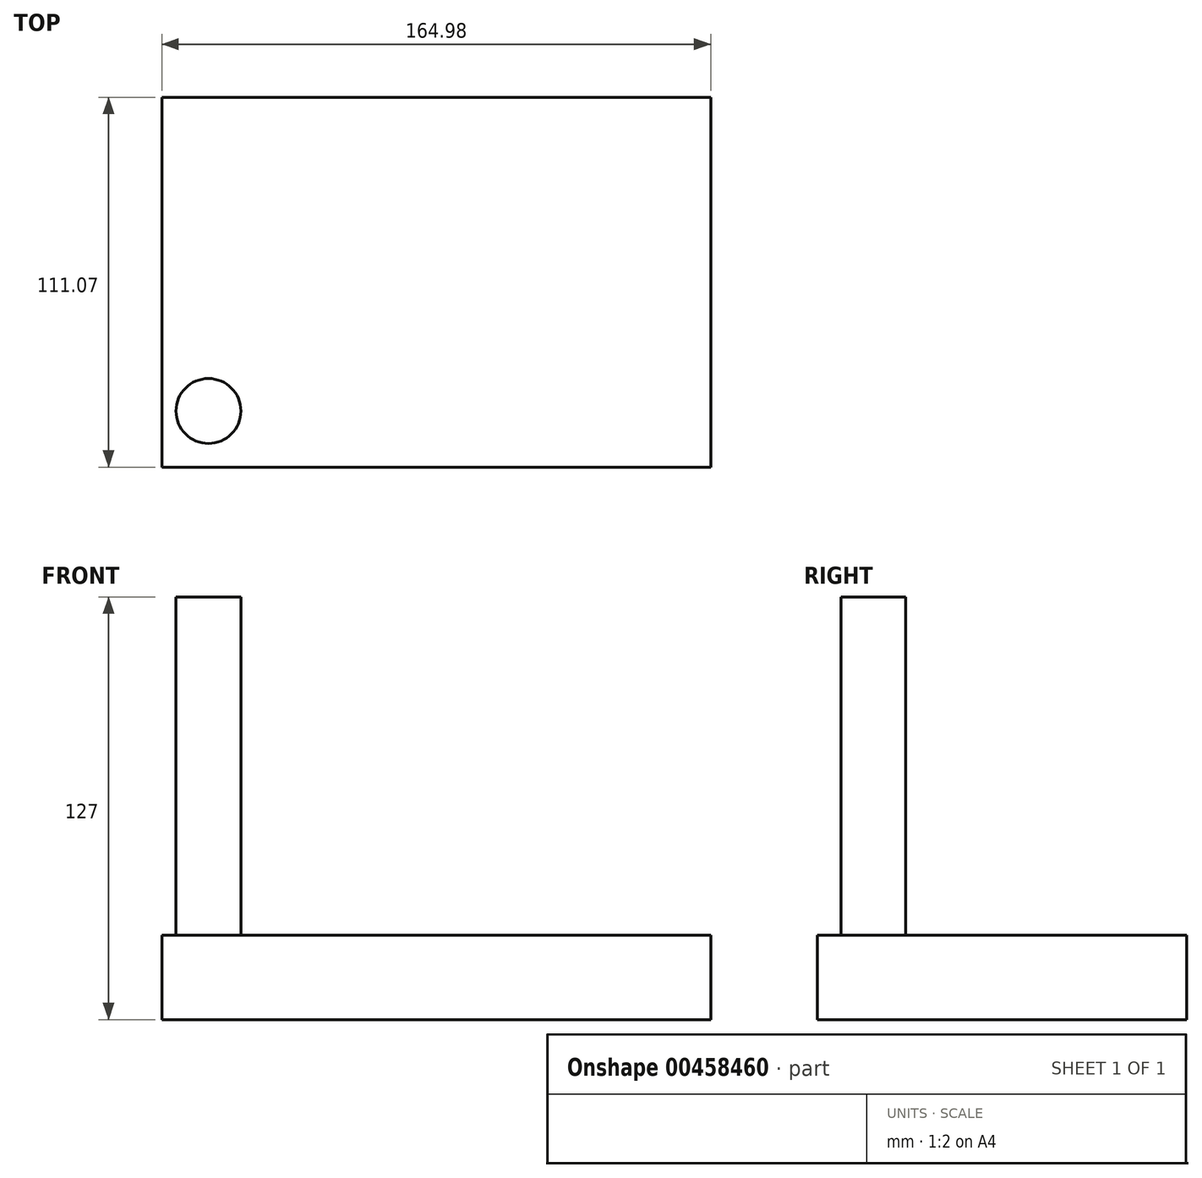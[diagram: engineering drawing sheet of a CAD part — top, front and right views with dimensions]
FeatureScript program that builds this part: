
annotation { "Feature Type Name" : "Feature", "Feature Type Description" : "" }
export const myFeature = defineFeature(function(context is Context, id is Id, definition is map)
    precondition{}
    {
        {
            var Q0;
            Q0=qCreatedBy(makeId("Top.planeOp"),FACE);
            var sketch = newSketch(context, id + "F0", { "sketchPlane" : qUnion([Q0])});
            skLineSegment(sketch, "E0.bottom", {"start": v(-111.35, 46.67) * mm, "end": v(53.63, 46.67) * mm});
            skLineSegment(sketch, "E0.top", {"start": v(-111.35, -64.4) * mm, "end": v(53.63, -64.4) * mm});
            skLineSegment(sketch, "E0.left", {"start": v(-111.35, 46.67) * mm, "end": v(-111.35, -64.4) * mm});
            skLineSegment(sketch, "E0.right", {"start": v(53.63, 46.67) * mm, "end": v(53.63, -64.4) * mm});
            skSolve(sketch);
        }
        {
            var Q0;
            Q0 = qSketchRegion(id + "F0", true);
            extrude(context, id + "F1", {"entities" : qUnion([Q0]), "depth" : 25.4 * mm});
        }
        {
            var Q0;
            Q0=makeQuery(id+"F1.opExtrude","CAP_FACE",FACE,{"disambiguationData":[OSD([sQuery(id+"F0.wireOp",EDGE,"E0.bottom"),sQuery(id+"F0.wireOp",EDGE,"E0.top"),sQuery(id+"F0.wireOp",EDGE,"E0.left"),sQuery(id+"F0.wireOp",EDGE,"E0.right")])],"isStart":false});
            var sketch = newSketch(context, id + "F2", { "sketchPlane" : qUnion([Q0])});
            skCircle(sketch, "E1", {"center": v(-97.34, -47.55) * mm, "radius": 9.75 * mm});
            skCircle(sketch, "E2", {"center": v(34.27, -46) * mm, "radius": 9.75 * mm});
            skCircle(sketch, "E3", {"center": v(35.53, 28.41) * mm, "radius": 9.75 * mm});
            skCircle(sketch, "E4", {"center": v(-97.34, 35.89) * mm, "radius": 9.75 * mm});
            skSolve(sketch);
        }
        {
            var Q0;
            Q0=makeQuery(id+"F2.imprint","IMPRINT",FACE,{"disambiguationData":[TD([[makeQuery(id+"F2.imprint","IMPRINT",EDGE,{"derivedFrom":sQuery(id+"F2.wireOp",EDGE,"E1")}),1.0]])]});
            extrude(context, id + "F3", {"entities" : qUnion([Q0]), "operationType" : NewBodyOperationType.ADD, "depth" : 101.6 * mm});
        }
    });
